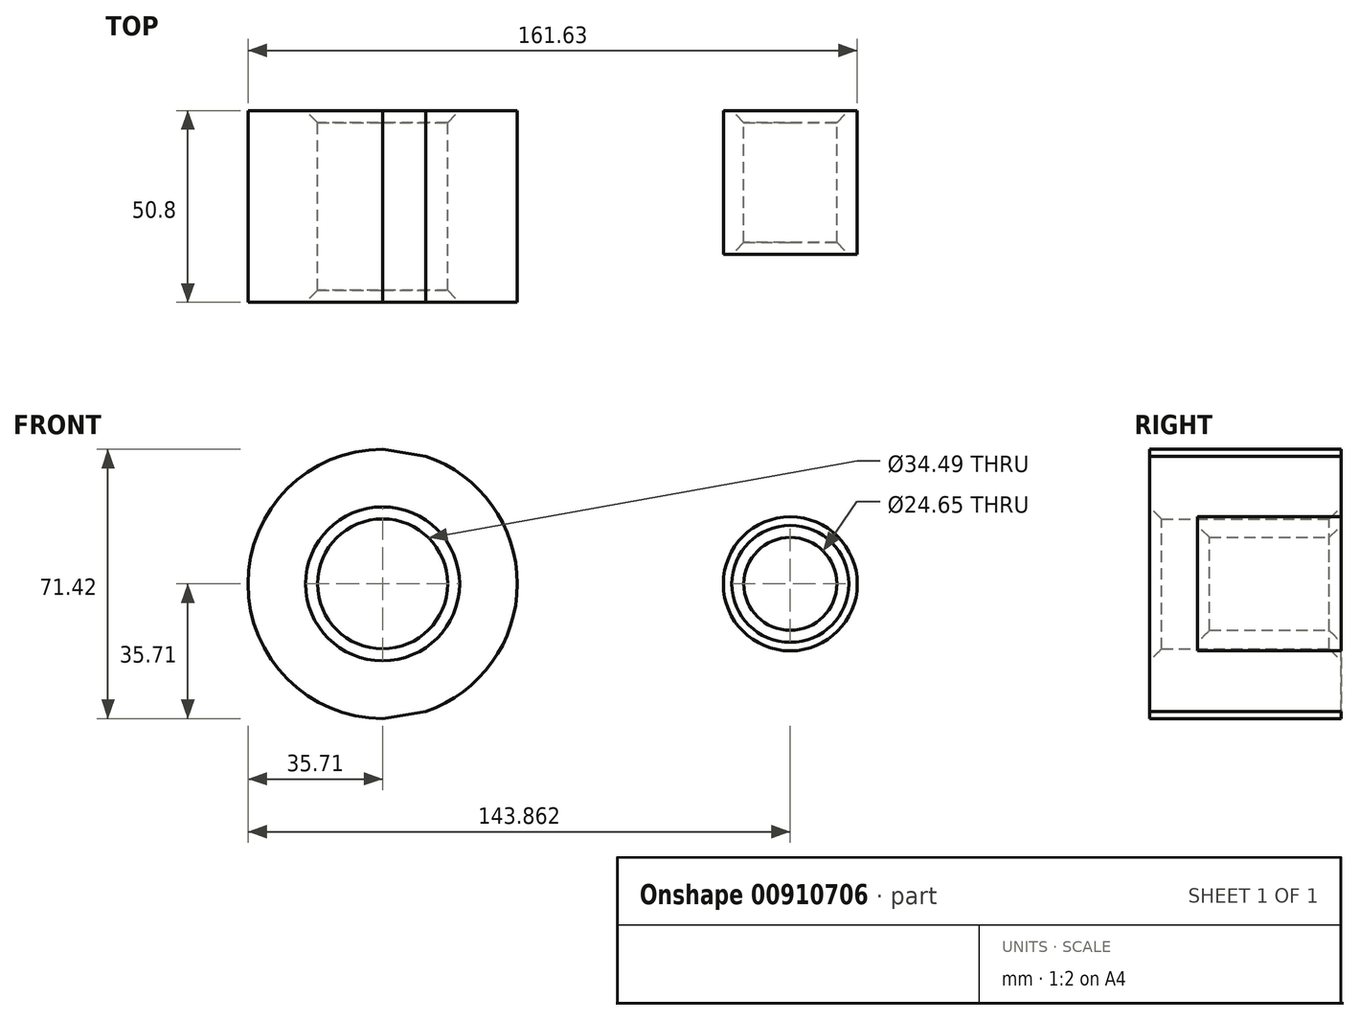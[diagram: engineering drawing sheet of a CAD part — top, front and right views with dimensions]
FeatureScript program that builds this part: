
annotation { "Feature Type Name" : "Feature", "Feature Type Description" : "" }
export const myFeature = defineFeature(function(context is Context, id is Id, definition is map)
    precondition{}
    {
        {
            var Q0;
            Q0=qCreatedBy(makeId("Front.planeOp"),FACE);
            var sketch = newSketch(context, id + "F0", { "sketchPlane" : qUnion([Q0])});
            skCircle(sketch, "E0", {"center": v(0, 0) * mm, "radius": 35.71 * mm});
            skCircle(sketch, "E1", {"center": v(108.15, 0) * mm, "radius": 17.77 * mm});
            skLineSegment(sketch, "E2", {"start": v(0, 35.71) * mm, "end": v(111.02, 17.54) * mm});
            skLineSegment(sketch, "E3", {"start": v(0, -35.71) * mm, "end": v(111.02, -17.54) * mm});
            skCircle(sketch, "E4", {"center": v(0, 0) * mm, "radius": 17.25 * mm});
            skCircle(sketch, "E5", {"center": v(108.15, 0) * mm, "radius": 12.32 * mm});
            skSolve(sketch);
        }
        {
            var Q0;
            {var subQ0=sQuery(id+"F0.wireOp",EDGE,"E2");var subQ1=sQuery(id+"F0.wireOp",EDGE,"E0");var subQ2=makeQuery(id+"F0.imprint","INTERSECT",VERTEX,{"disambiguationData":[OD(1.0)],"derivedFrom":[subQ1,subQ0]});Q0=makeQuery(id+"F0.imprint","IMPRINT",FACE,{"disambiguationData":[TD([[makeQuery(id+"F0.imprint","IMPRINT",EDGE,{"disambiguationData":[TD([[subQ2,1.0]])],"derivedFrom":subQ1}),-1.0]])]});}
            var Q1;
            Q1=makeQuery(id+"F0.imprint","IMPRINT",FACE,{"disambiguationData":[TD([[makeQuery(id+"F0.imprint","IMPRINT",EDGE,{"derivedFrom":sQuery(id+"F0.wireOp",EDGE,"E5")}),-1.0]])]});
            extrude(context, id + "F1", {"entities" : qUnion([Q0, Q1]), "depth" : 38.1 * mm, "offsetDistance" : 25.4 * mm});
        }
        {
            var Q0;
            Q0=makeQuery(id+"F0.imprint","IMPRINT",FACE,{"disambiguationData":[TD([[makeQuery(id+"F0.imprint","IMPRINT",EDGE,{"derivedFrom":sQuery(id+"F0.wireOp",EDGE,"E4")}),-1.0]])]});
            extrude(context, id + "F2", {"entities" : qUnion([Q0]), "operationType" : NewBodyOperationType.ADD, "depth" : 50.8 * mm, "offsetDistance" : 25.4 * mm});
        }
        {
            var Q0;
            Q0=makeQuery(id+"F2.opExtrude","CAP_EDGE",EDGE,{"disambiguationData":[OSD([sQuery(id+"F0.wireOp",EDGE,"E4")])],"isStart":false});
            var Q1;
            {var subQ0=sQuery(id+"F0.wireOp",EDGE,"E0");Q1=makeQuery(id+"F2.opExtrude","CAP_EDGE",EDGE,{"disambiguationData":[OSD([subQ0]),TDD([makeQuery(id+"F0.imprint","IMPRINT",EDGE,{"disambiguationData":[TD([[makeQuery(id+"F0.imprint","INTERSECT",VERTEX,{"disambiguationData":[OD(1.0)],"derivedFrom":[subQ0,sQuery(id+"F0.wireOp",EDGE,"E2")]}),1.0]])],"derivedFrom":subQ0})])],"isStart":false});}
            var Q2;
            Q2=makeQuery(id+"F1.opExtrude","CAP_EDGE",EDGE,{"disambiguationData":[OSD([sQuery(id+"F0.wireOp",EDGE,"E5")])],"isStart":false});
            chamfer(context, id + "F3", {"entities" : qUnion([Q0, Q1, Q2]), "width" : 3.17 * mm, "tangentPropagation" : true});
        }
        {
            var Q0;
            Q0=makeQuery(id+"F1.opExtrude","CAP_EDGE",EDGE,{"disambiguationData":[OSD([sQuery(id+"F0.wireOp",EDGE,"E5")])],"isStart":true});
            var Q1;
            Q1=makeQuery(id+"F2.opExtrude","CAP_EDGE",EDGE,{"disambiguationData":[OSD([sQuery(id+"F0.wireOp",EDGE,"E4")])],"isStart":true});
            chamfer(context, id + "F4", {"entities" : qUnion([Q0, Q1]), "width" : 3.17 * mm, "tangentPropagation" : true});
        }
    });
